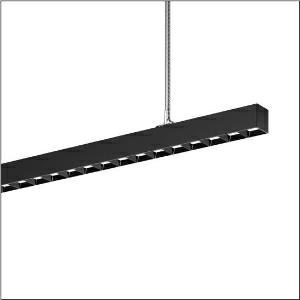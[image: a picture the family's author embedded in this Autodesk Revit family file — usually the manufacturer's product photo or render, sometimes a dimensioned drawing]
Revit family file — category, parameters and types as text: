
# Revit family: silica_r__21_51mx31tctdb_123f
name_source: partatom
category: Lighting Fixtures
units: mm (PartAtom-declared; Revit-internal decimal feet)

## family parameters
Cut with Voids When Loaded = No
Host = Face
Light Source = No
Part Type = Normal
Room Calculation Point = No
Round Connector Dimension = Use Diameter
Shared = No

## types (1)
- --- (1 x LED, 15550 lm, 133.9 W, 6500K)
    Apparent Load = 134 VA
    CIE Flux Codes = 85 99 100 60 100
    Color Rendering = 80
    Color Temperature = 6500K
    Default Elevation = 1800 mm
    Description = Silica® 21, office luminaire, primary light control with darklight reflector, of PMMA, black, CAT 2 (L<= 3000cd/m²), light emission: direct/indirect distribution, primary light characteristic: symmetric, installation type: suspended mounting, LED, rated luminous flux: 15.550lm, luminous efficacy: 111lm/W, light colour: 8tw, colour temperature: 2700..6500K, control gear: ECG DALI, with terminal, 3+2-pole, max. 2.5mm², mains connection: 220..240V, AC, 50/60Hz, rated input power: 140.6W, luminaire housing, of aluminium, jet black (RAL 9005), length: 3.004mm, width: 53mm, height: 53mm, protection rating (complete): IP20, insulation class (complete): insulation class I (protective earthing), certification: CE, permissible operating ambient temperature: 0..+35°C, standard: EN 50419, packaging unit: 1 piece
    Height = 53 mm
    Lamp = 1 x LED
    Lamp Light Flux = 15550 lm
    Lamp Power = 133.9 W
    Lamp count = 1
    Length = 3004 mm
    Luminous efficacy = 116 lm/W
    Manufacturer = Siteco
    ModVariant = No
    Model = 51MX31TCTDB
    Mounting Place = Ceiling
    Mounting Type = Pendant
    Number of Poles = 1
    OnlyDefault = Yes
    Power Factor = 1
    Product Name = Silica® 21
    Product group = office luminaire | ceiling pendant
    ProductGroupID = 902
    Protection Class = Protection class I
    Protection Degree = IP 20
    RLX_Detail_Level = 1
    RLX_Emergency_Light_Flux = 0 lm
    RLX_Emergency_Type = 0
    RLX_Emergency_Type_DB = No
    RlxData = <blob elided: 65645 chars, md5=1b7716ed>
    Socket = socket
    Standby Power = 0 W
    System Light Flux = 15550 lm
    System Power = 134 W
    Type Comments = individual setting
    Type Image = l_1297774.jpg
    URL = http://relux.com
    VarID = @adj_071203
    Voltage = 0 V
    Weight = 0.00 kg
    Width = 53 mm

## geometry (parser evidence)
native form markers: Blend x4, Sweep x11
no freeform markers — native parametric forms only
